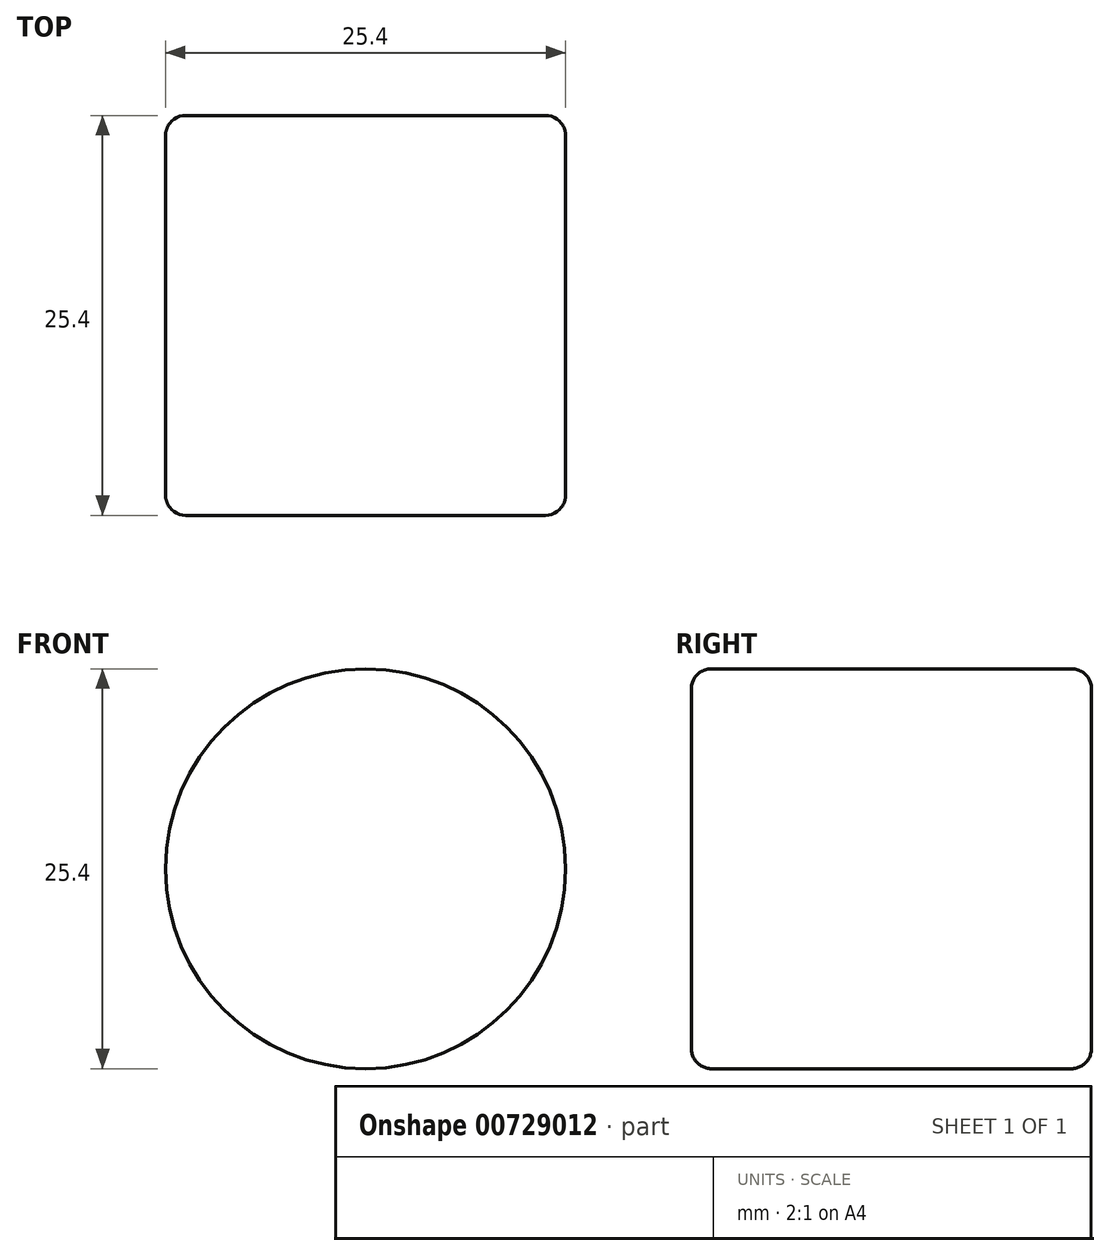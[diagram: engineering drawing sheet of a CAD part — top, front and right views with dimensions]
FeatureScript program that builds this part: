
annotation { "Feature Type Name" : "Feature", "Feature Type Description" : "" }
export const myFeature = defineFeature(function(context is Context, id is Id, definition is map)
    precondition{}
    {
        {
            var Q0;
            Q0=qCreatedBy(makeId("Front.planeOp"),FACE);
            var sketch = newSketch(context, id + "F0", { "sketchPlane" : qUnion([Q0])});
            skCircle(sketch, "E0", {"center": v(0, 0) * mm, "radius": 12.7 * mm});
            skSolve(sketch);
        }
        {
            var Q0;
            Q0 = qSketchRegion(id + "F0", true);
            extrude(context, id + "F1", {"entities" : qUnion([Q0]), "oppositeDirection" : true, "depth" : 25.4 * mm, "offsetDistance" : 25.4 * mm});
        }
        {
            var Q0;
            Q0=makeQuery(id+"F1.opExtrude","CAP_EDGE",EDGE,{"disambiguationData":[OSD([sQuery(id+"F0.wireOp",EDGE,"E0")])],"isStart":true});
            var Q1;
            Q1=makeQuery(id+"F1.opExtrude","CAP_EDGE",EDGE,{"disambiguationData":[OSD([sQuery(id+"F0.wireOp",EDGE,"E0")])],"isStart":false});
            fillet(context, id + "F2", {"entities" : qUnion([Q0, Q1]), "radius" : 1.27 * mm, "tangentPropagation" : true, "allowEdgeOverflow" : false});
        }
    });
